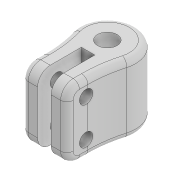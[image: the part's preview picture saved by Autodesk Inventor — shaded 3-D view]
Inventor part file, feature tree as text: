
AUTODESK INVENTOR PART (.ipt)
format: ipt  version: 2022 (Build 260153000, 153)  size: 222,208 bytes
history: native  units: mm
features: extrude x4, sketch x3, fillet x3
ambient origin geometry x8: Origin, YZ Plane, XZ Plane, XY Plane, X Axis, Y Axis, Z Axis, Center Point
bodies: Solid1 (feature_tree)
feature tree (10):
  extrude  "Extrusion1"  Depth=9.0mm
  sketch  "Sketch2"  dims[d2=11.0mm d3=0.0mm d4=2.15mm]
  extrude  "Extrusion2"  Depth=11.0mm
  extrude  "Extrusion4"  Depth=20.0mm
  extrude  "Extrusion3"  Depth=20.0mm
  fillet  "Fillet5"  Radius=10.0mm
  fillet  "Fillet3"  Radius=11.0mm
  fillet  "Fillet4"  Radius=2.1mm
  sketch  "Sketch1"  dims[d0=3.1mm d1=9.0mm]
  sketch  "Sketch3"  dims[d5=1.075mm d6=2.5mm d7=2.5mm d8=10.0mm d9=11.0mm d10=0.0mm d11=2.1mm d12=2.1mm d13=2.0mm d14=2.0mm d15=1.5mm d16=1.5mm d17=11.0mm d18=0.0mm d21=2.0mm d22=1.0mm d23=11.0mm d24=0.0mm d25=1.5mm d26=20.0mm]
